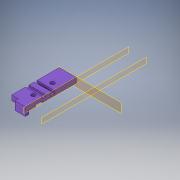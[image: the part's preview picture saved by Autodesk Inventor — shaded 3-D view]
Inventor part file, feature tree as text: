
AUTODESK INVENTOR PART (.ipt)
format: ipt  version: 2018.2 (Build 222227000, 227)  size: 312,832 bytes
history: native  units: in
note: dims shown in document units (in); Inventor stores cm internally (conversion verified against a paired STEP export)
features: extrude x12, sketch x11, mirror x10, split x3, plane x2
ambient origin geometry x8: Origin, YZ Plane, XZ Plane, XY Plane, X Axis, Y Axis, Z Axis, Center Point
bodies: Solid1 (feature_tree)
feature tree (38):
  extrude  "Extrusion1"  Depth=0.375in
  extrude  "Extrusion2"  Depth=0.75in
  mirror  "Mirror1"
  extrude  "Extrusion3"  Depth=7.0in TaperAngle=0.0deg
  extrude  "Extrusion4"  Depth=0.5in TaperAngle=0.0deg
  mirror  "Mirror2"
  extrude  "Extrusion5"  Depth=0.25in
  mirror  "Mirror3"
  extrude  "Extrusion8"  Depth=1.0in TaperAngle=0.0deg
  mirror  "Mirror4"
  plane  "Work Plane1"
  extrude  "Extrusion9"  Depth=1.25in
  mirror  "Mirror5"
  extrude  "Extrusion10"  Depth=0.5in TaperAngle=0.0deg
  mirror  "Mirror6"
  extrude  "Extrusion11"  Depth=0.25in
  extrude  "Extrusion12"  Depth=0.5in TaperAngle=0.0deg
  mirror  "Mirror7"
  mirror  "Mirror8"
  extrude  "Extrusion13"  Depth=0.25in
  extrude  "Extrusion14"  Depth=0.25in
  mirror  "Mirror9"
  mirror  "Mirror10"
  split  "Split3"
  split  "Split4"
  plane  "Work Plane2"
  split  "Split5"
  sketch  "Sketch4"  dims[d0=0.375in d1=0.375in]
  sketch  "Sketch6"  dims[d6=2.5in d8=0.75in]
  sketch  "Sketch7"  dims[d9=7.0in d10=14.0in d11=0.0in]
  sketch  "Sketch9"  dims[d12=0.875in d13=0.5in d14=0.0in]
  sketch  "Sketch12"  dims[d16=0.5in d18=0.25in]
  sketch  "Sketch13"  dims[d19=3.5in d20=1.0in d21=0.0in]
  sketch  "Sketch14"  dims[d22=1.75in d23=1.25in]
  sketch  "Sketch16"  dims[d24=1.0in d25=0.5in d26=0.0in]
  sketch  "Sketch17"  dims[d28=0.5in d29=0.25in]
  sketch  "Sketch18"  dims[d30=2.0in d31=0.5in d32=0.0in]
  sketch  "Sketch19"  dims[d46=3.5in d47=0.1875in d48=0.25in d49=0.25in d50=0.344in d51=0.5in d52=0.0in d53=-5.125in d54=1.0in d55=0.25in d56=1.0in d57=10.25in d58=0.0in d59=1.0in d60=0.25in d61=1.0in d62=9.0in d63=0.0in d71=0.266in d72=2.0in d73=0.5in d74=9.0in d75=0.0in d76=0.6in d77=0.25in d78=0.0in d79=0.266in d80=1.0in d81=0.25in d82=0.0in d83=0.6in d84=0.25in d85=0.0in d86=-2.625in]
